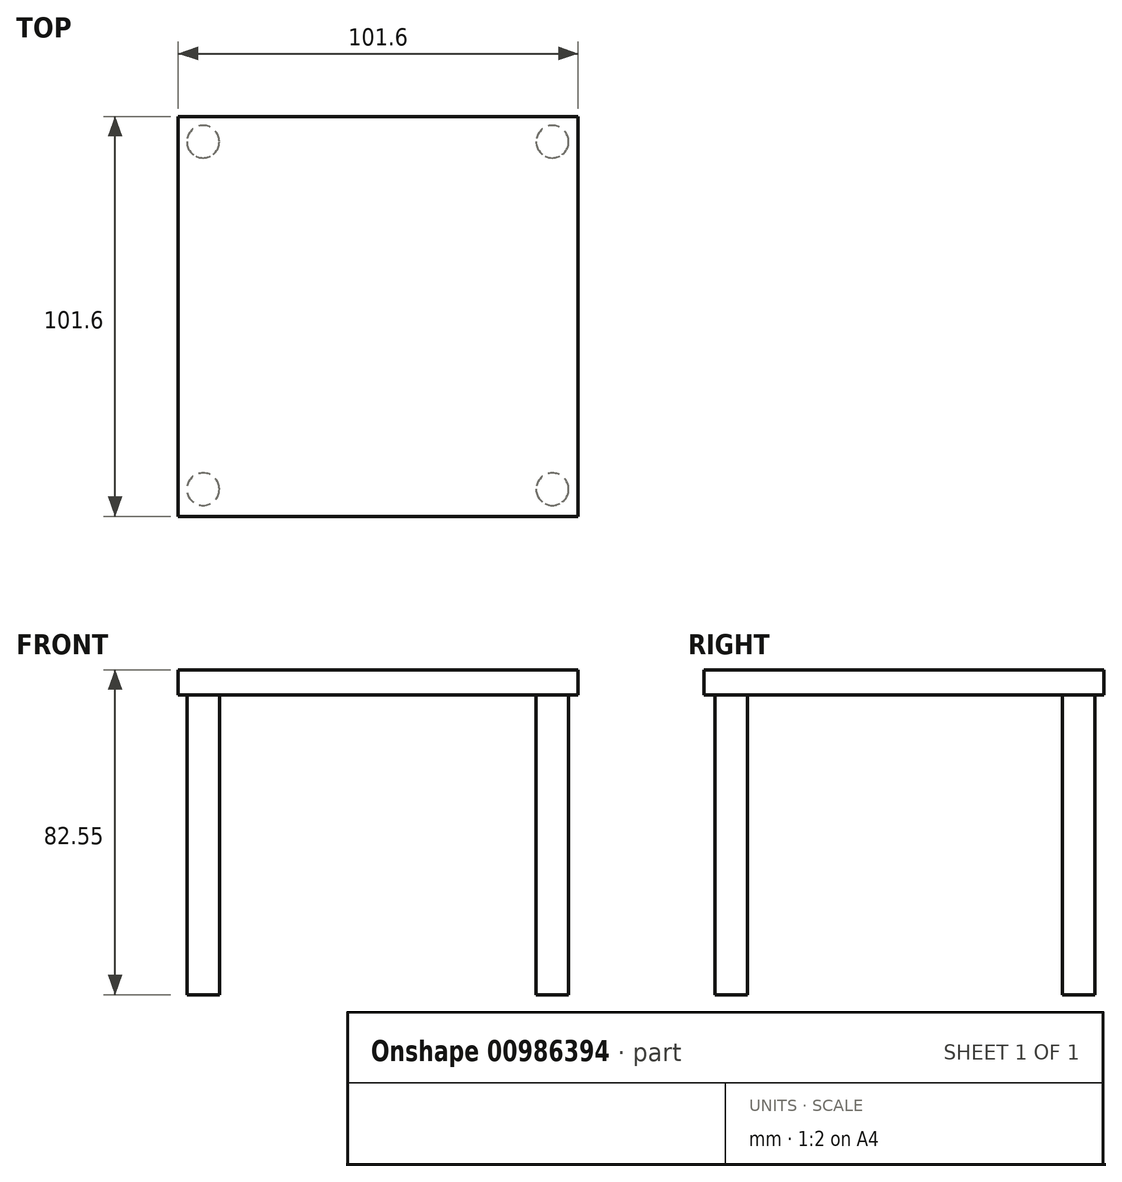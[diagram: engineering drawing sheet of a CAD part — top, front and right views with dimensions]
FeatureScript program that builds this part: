
annotation { "Feature Type Name" : "Feature", "Feature Type Description" : "" }
export const myFeature = defineFeature(function(context is Context, id is Id, definition is map)
    precondition{}
    {
        {
            var Q0;
            Q0=qCreatedBy(makeId("Top.planeOp"),FACE);
            var sketch = newSketch(context, id + "F0", { "sketchPlane" : qUnion([Q0])});
            skLineSegment(sketch, "E0.bottom", {"start": v(50.8, -50.8) * mm, "end": v(-50.8, -50.8) * mm});
            skLineSegment(sketch, "E0.top", {"start": v(50.8, 50.8) * mm, "end": v(-50.8, 50.8) * mm});
            skLineSegment(sketch, "E0.left", {"start": v(50.8, -50.8) * mm, "end": v(50.8, 50.8) * mm});
            skLineSegment(sketch, "E0.right", {"start": v(-50.8, -50.8) * mm, "end": v(-50.8, 50.8) * mm});
            skPoint(sketch, "E0.middle", {"position": v(0, 0) * mm});
            skSolve(sketch);
        }
        {
            var Q0;
            Q0 = qSketchRegion(id + "F0", true);
            extrude(context, id + "F1", {"entities" : qUnion([Q0]), "depth" : 6.35 * mm, "offsetDistance" : 25.4 * mm});
        }
        {
            var Q0;
            Q0=makeQuery(id+"F1.opExtrude","CAP_FACE",FACE,{"disambiguationData":[OSD([sQuery(id+"F0.wireOp",EDGE,"E0.bottom"),sQuery(id+"F0.wireOp",EDGE,"E0.top"),sQuery(id+"F0.wireOp",EDGE,"E0.left"),sQuery(id+"F0.wireOp",EDGE,"E0.right")])],"isStart":true});
            var sketch = newSketch(context, id + "F2", { "sketchPlane" : qUnion([Q0])});
            skCircle(sketch, "E1", {"center": v(-44.47, 43.92) * mm, "radius": 4.12 * mm});
            skCircle(sketch, "E2", {"center": v(44.25, 43.92) * mm, "radius": 4.12 * mm});
            skCircle(sketch, "E3", {"center": v(44.25, -44.36) * mm, "radius": 4.12 * mm});
            skCircle(sketch, "E4", {"center": v(-44.47, -44.36) * mm, "radius": 4.12 * mm});
            skSolve(sketch);
        }
        {
            var Q0;
            Q0=makeQuery(id+"F2.imprint","IMPRINT",FACE,{"disambiguationData":[TD([[makeQuery(id+"F2.imprint","IMPRINT",EDGE,{"derivedFrom":sQuery(id+"F2.wireOp",EDGE,"E1")}),1.0]])]});
            var Q1;
            Q1=makeQuery(id+"F2.imprint","IMPRINT",FACE,{"disambiguationData":[TD([[makeQuery(id+"F2.imprint","IMPRINT",EDGE,{"derivedFrom":sQuery(id+"F2.wireOp",EDGE,"E2")}),1.0]])]});
            var Q2;
            Q2=makeQuery(id+"F2.imprint","IMPRINT",FACE,{"disambiguationData":[TD([[makeQuery(id+"F2.imprint","IMPRINT",EDGE,{"derivedFrom":sQuery(id+"F2.wireOp",EDGE,"E3")}),1.0]])]});
            var Q3;
            Q3=makeQuery(id+"F2.imprint","IMPRINT",FACE,{"disambiguationData":[TD([[makeQuery(id+"F2.imprint","IMPRINT",EDGE,{"derivedFrom":sQuery(id+"F2.wireOp",EDGE,"E4")}),1.0]])]});
            extrude(context, id + "F3", {"entities" : qUnion([Q0, Q1, Q2, Q3]), "operationType" : NewBodyOperationType.ADD, "depth" : 76.2 * mm, "offsetDistance" : 25.4 * mm});
        }
    });
